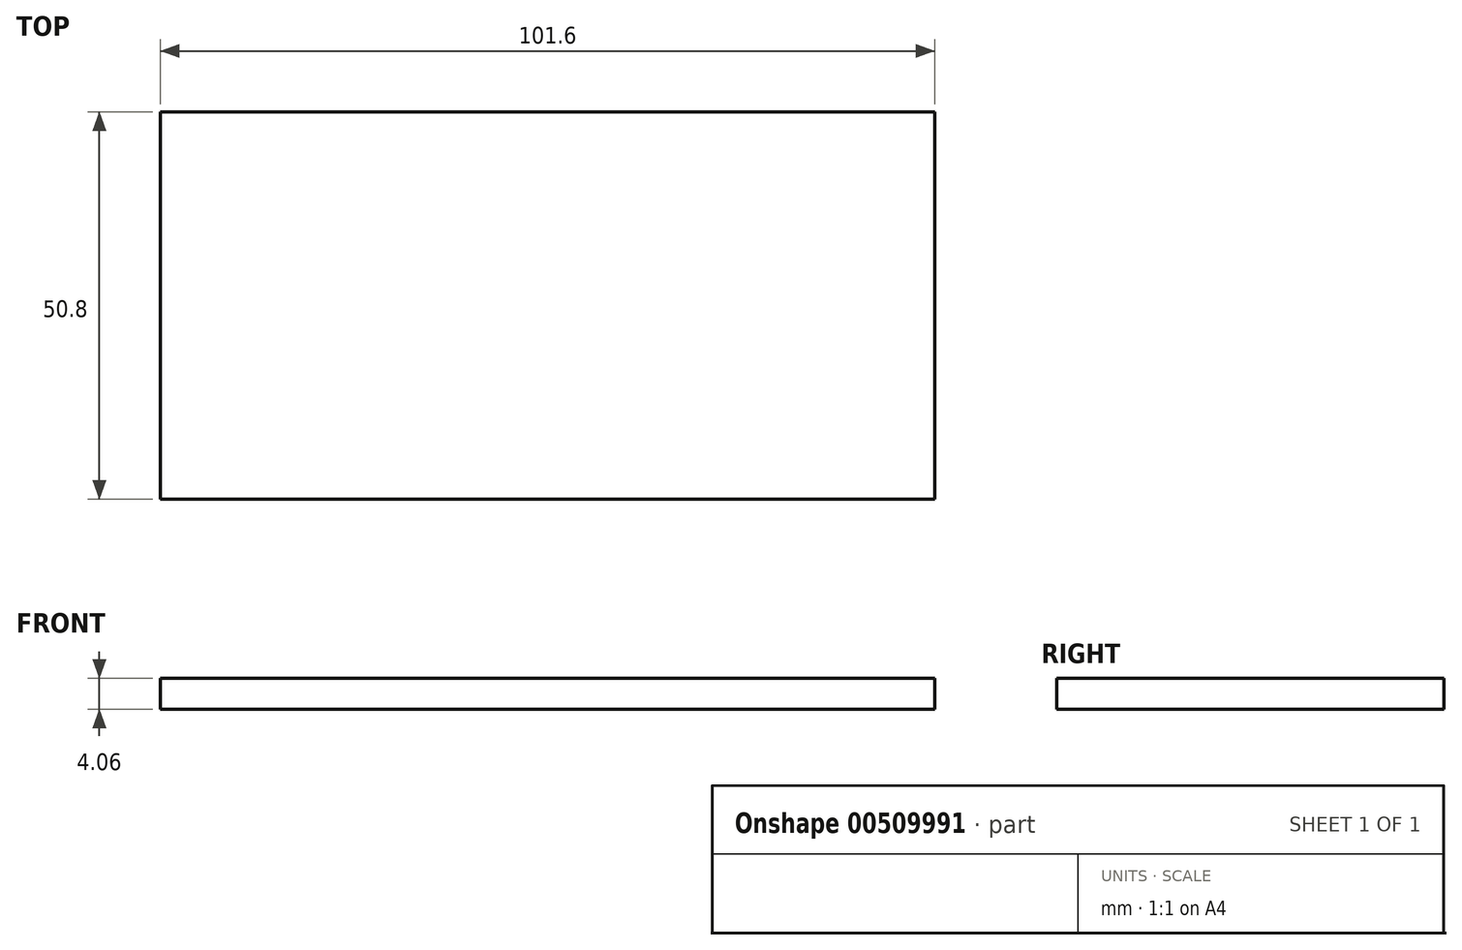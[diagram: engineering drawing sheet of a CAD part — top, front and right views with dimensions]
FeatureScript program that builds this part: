
annotation { "Feature Type Name" : "Feature", "Feature Type Description" : "" }
export const myFeature = defineFeature(function(context is Context, id is Id, definition is map)
    precondition{}
    {
        {
            var Q0;
            Q0=qCreatedBy(makeId("Top.planeOp"),FACE);
            var sketch = newSketch(context, id + "F0", { "sketchPlane" : qUnion([Q0])});
            skLineSegment(sketch, "E0.bottom", {"start": v(-48.66, 50.8) * mm, "end": v(52.94, 50.8) * mm});
            skLineSegment(sketch, "E0.top", {"start": v(-48.66, 0) * mm, "end": v(52.94, 0) * mm});
            skLineSegment(sketch, "E0.left", {"start": v(-48.66, 50.8) * mm, "end": v(-48.66, 0) * mm});
            skLineSegment(sketch, "E0.right", {"start": v(52.94, 50.8) * mm, "end": v(52.94, 0) * mm});
            skSolve(sketch);
        }
        {
            var Q0;
            Q0=makeQuery(id+"F0.imprint","IMPRINT",FACE,{"disambiguationData":[TD([[makeQuery(id+"F0.imprint","IMPRINT",EDGE,{"derivedFrom":sQuery(id+"F0.wireOp",EDGE,"E0.bottom")}),-1.0]])]});
            extrude(context, id + "F1", {"entities" : qUnion([Q0]), "depth" : 4.06 * mm, "offsetDistance" : 25.4 * mm});
        }
    });
